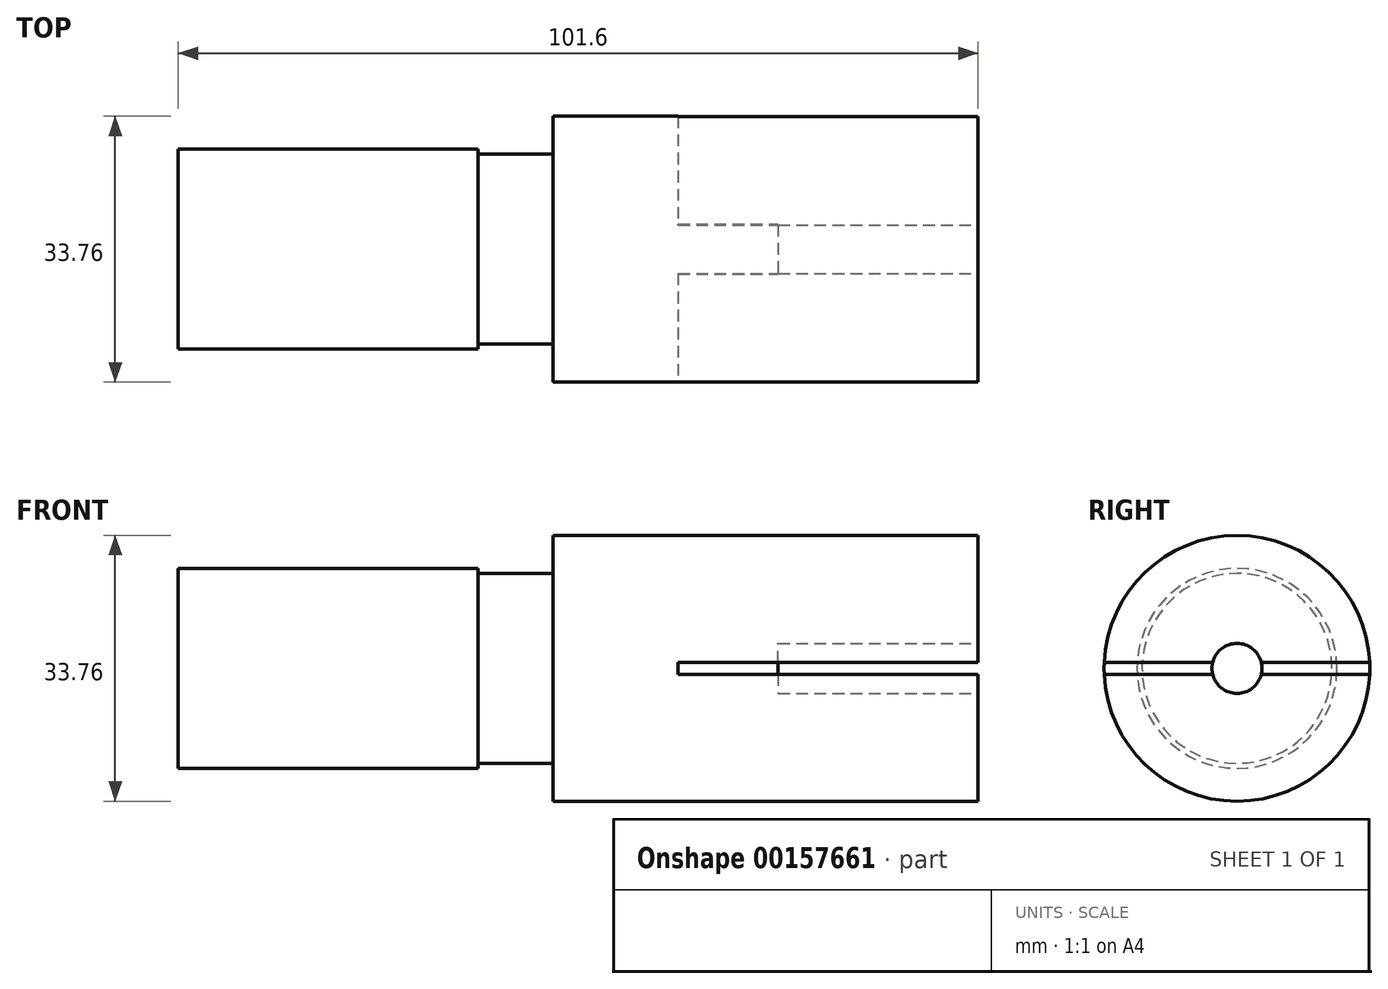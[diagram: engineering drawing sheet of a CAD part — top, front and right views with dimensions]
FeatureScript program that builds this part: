
annotation { "Feature Type Name" : "Feature", "Feature Type Description" : "" }
export const myFeature = defineFeature(function(context is Context, id is Id, definition is map)
    precondition{}
    {
        {
            var Q0;
            Q0=qCreatedBy(makeId("Right.planeOp"),FACE);
            var sketch = newSketch(context, id + "F0", { "sketchPlane" : qUnion([Q0])});
            skCircle(sketch, "E0", {"center": v(0, 0) * mm, "radius": 12.07 * mm});
            skSolve(sketch);
        }
        {
            var Q0;
            Q0=makeQuery(id+"F0.imprint","IMPRINT",FACE,{"disambiguationData":[TD([[makeQuery(id+"F0.imprint","IMPRINT",EDGE,{"derivedFrom":sQuery(id+"F0.wireOp",EDGE,"E0")}),1.0]])]});
            extrude(context, id + "F1", {"entities" : qUnion([Q0]), "depth" : 9.52 * mm});
        }
        {
            var Q0;
            Q0=makeQuery(id+"F1.opExtrude","CAP_FACE",FACE,{"disambiguationData":[OSD([sQuery(id+"F0.wireOp",EDGE,"E0")])],"isStart":false});
            var sketch = newSketch(context, id + "F2", { "sketchPlane" : qUnion([Q0])});
            skCircle(sketch, "E1", {"center": v(0, 0) * mm, "radius": 16.88 * mm});
            skSolve(sketch);
        }
        {
            var Q0;
            Q0=makeQuery(id+"F2.imprint","IMPRINT",FACE,{"disambiguationData":[TD([[makeQuery(id+"F2.imprint","IMPRINT",EDGE,{"derivedFrom":makeQuery(id+"F1.opExtrude","CAP_EDGE",EDGE,{"disambiguationData":[OSD([sQuery(id+"F0.wireOp",EDGE,"E0")])],"isStart":false})}),1.0]])]});
            var Q1;
            Q1=makeQuery(id+"F2.imprint","IMPRINT",FACE,{"disambiguationData":[TD([[makeQuery(id+"F2.imprint","IMPRINT",EDGE,{"derivedFrom":sQuery(id+"F2.wireOp",EDGE,"E1")}),1.0]])]});
            extrude(context, id + "F3", {"entities" : qUnion([Q0, Q1]), "operationType" : NewBodyOperationType.ADD, "depth" : 53.97 * mm});
        }
        {
            var Q0;
            Q0=makeQuery(id+"F1.opExtrude","CAP_FACE",FACE,{"disambiguationData":[OSD([sQuery(id+"F0.wireOp",EDGE,"E0")])],"isStart":true});
            var sketch = newSketch(context, id + "F4", { "sketchPlane" : qUnion([Q0])});
            skCircle(sketch, "E2", {"center": v(0, 0) * mm, "radius": 12.7 * mm});
            skSolve(sketch);
        }
        {
            var Q0;
            Q0=makeQuery(id+"F4.imprint","IMPRINT",FACE,{"disambiguationData":[TD([[makeQuery(id+"F4.imprint","IMPRINT",EDGE,{"derivedFrom":makeQuery(id+"F1.opExtrude","CAP_EDGE",EDGE,{"disambiguationData":[OSD([sQuery(id+"F0.wireOp",EDGE,"E0")])],"isStart":true})}),-1.0]])]});
            var Q1;
            Q1=makeQuery(id+"F4.imprint","IMPRINT",FACE,{"disambiguationData":[TD([[makeQuery(id+"F4.imprint","IMPRINT",EDGE,{"derivedFrom":sQuery(id+"F4.wireOp",EDGE,"E2")}),1.0]])]});
            extrude(context, id + "F5", {"entities" : qUnion([Q0, Q1]), "operationType" : NewBodyOperationType.ADD, "depth" : 38.1 * mm});
        }
        {
            var Q0;
            Q0=makeQuery(id+"F3.opExtrude","CAP_FACE",FACE,{"disambiguationData":[OSD([sQuery(id+"F2.wireOp",EDGE,"E1")])],"isStart":false});
            var sketch = newSketch(context, id + "F6", { "sketchPlane" : qUnion([Q0])});
            skCircle(sketch, "E3", {"center": v(0, 0) * mm, "radius": 3.18 * mm});
            skSolve(sketch);
        }
        {
            var Q0;
            Q0=makeQuery(id+"F6.imprint","IMPRINT",FACE,{"disambiguationData":[TD([[makeQuery(id+"F6.imprint","IMPRINT",EDGE,{"derivedFrom":sQuery(id+"F6.wireOp",EDGE,"E3")}),1.0]])]});
            extrude(context, id + "F7", {"entities" : qUnion([Q0]), "operationType" : NewBodyOperationType.REMOVE, "oppositeDirection" : true, "depth" : 25.4 * mm});
        }
        {
            var Q0;
            Q0=makeQuery(id+"F3.opExtrude","CAP_FACE",FACE,{"disambiguationData":[OSD([sQuery(id+"F2.wireOp",EDGE,"E1")])],"isStart":false});
            var sketch = newSketch(context, id + "F8", { "sketchPlane" : qUnion([Q0])});
            skLineSegment(sketch, "E4.bottom", {"start": v(18.8, -0.74) * mm, "end": v(-18.8, -0.74) * mm});
            skLineSegment(sketch, "E4.top", {"start": v(18.8, 0.74) * mm, "end": v(-18.8, 0.74) * mm});
            skLineSegment(sketch, "E4.left", {"start": v(18.8, -0.74) * mm, "end": v(18.8, 0.74) * mm});
            skLineSegment(sketch, "E4.right", {"start": v(-18.8, -0.74) * mm, "end": v(-18.8, 0.74) * mm});
            skPoint(sketch, "E4.middle", {"position": v(0, 0) * mm});
            skSolve(sketch);
        }
        {
            var Q0;
            {var subQ0=sQuery(id+"F8.wireOp",EDGE,"E4.bottom");var subQ1=makeQuery(id+"F3.opExtrude","CAP_EDGE",EDGE,{"disambiguationData":[OSD([sQuery(id+"F2.wireOp",EDGE,"E1")])],"isStart":false});var subQ2=makeQuery(id+"F8.imprint","INTERSECT",VERTEX,{"disambiguationData":[OD(1.0)],"derivedFrom":[subQ1,subQ0]});Q0=makeQuery(id+"F8.imprint","IMPRINT",FACE,{"disambiguationData":[TD([[makeQuery(id+"F8.imprint","IMPRINT",EDGE,{"disambiguationData":[TD([[subQ2,1.0]])],"derivedFrom":subQ0}),-1.0]])]});}
            var Q1;
            {var subQ0=sQuery(id+"F8.wireOp",EDGE,"E4.bottom");var subQ1=makeQuery(id+"F3.opExtrude","CAP_EDGE",EDGE,{"disambiguationData":[OSD([sQuery(id+"F2.wireOp",EDGE,"E1")])],"isStart":false});var subQ2=makeQuery(id+"F8.imprint","INTERSECT",VERTEX,{"disambiguationData":[OD(0.0)],"derivedFrom":[subQ1,subQ0]});Q1=makeQuery(id+"F8.imprint","IMPRINT",FACE,{"disambiguationData":[TD([[makeQuery(id+"F8.imprint","IMPRINT",EDGE,{"disambiguationData":[TD([[subQ2,-1.0]])],"derivedFrom":subQ0}),-1.0]])]});}
            extrude(context, id + "F9", {"entities" : qUnion([Q0, Q1]), "operationType" : NewBodyOperationType.REMOVE, "oppositeDirection" : true, "depth" : 38.1 * mm});
        }
    });
